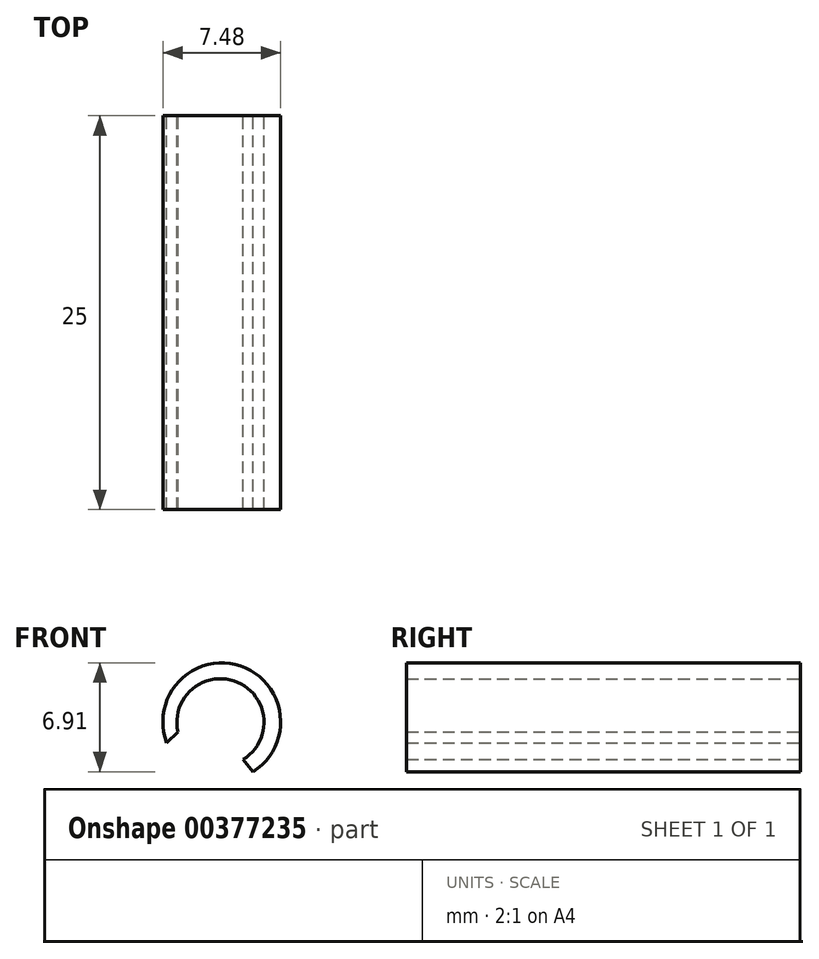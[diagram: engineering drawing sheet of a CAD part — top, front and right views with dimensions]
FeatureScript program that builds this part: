
annotation { "Feature Type Name" : "Feature", "Feature Type Description" : "" }
export const myFeature = defineFeature(function(context is Context, id is Id, definition is map)
    precondition{}
    {
        {
            var Q0;
            Q0=qCreatedBy(makeId("Front.planeOp"),FACE);
            var sketch = newSketch(context, id + "F0", { "sketchPlane" : qUnion([Q0])});
            skArc(sketch, "E0", {"start": v(5.48, -1.83) * mm, "mid": v(4.68, 4.88) * mm, "end": v(0, 0) * mm});
            skLineSegment(sketch, "E1", {"start": v(5.48, -1.83) * mm, "end": v(4.85, -1.06) * mm});
            skLineSegment(sketch, "E2", {"start": v(0, 0) * mm, "end": v(0.7, 0.7) * mm});
            skArc(sketch, "E3", {"start": v(4.85, -1.06) * mm, "mid": v(4.5, 3.85) * mm, "end": v(0.7, 0.7) * mm});
            skSolve(sketch);
        }
        {
            var Q0;
            Q0=makeQuery(id+"F0.imprint","IMPRINT",FACE,{"disambiguationData":[TD([[makeQuery(id+"F0.imprint","IMPRINT",EDGE,{"derivedFrom":sQuery(id+"F0.wireOp",EDGE,"E0")}),1.0]])]});
            extrude(context, id + "F1", {"entities" : qUnion([Q0]), "depth" : 25 * mm});
        }
    });
